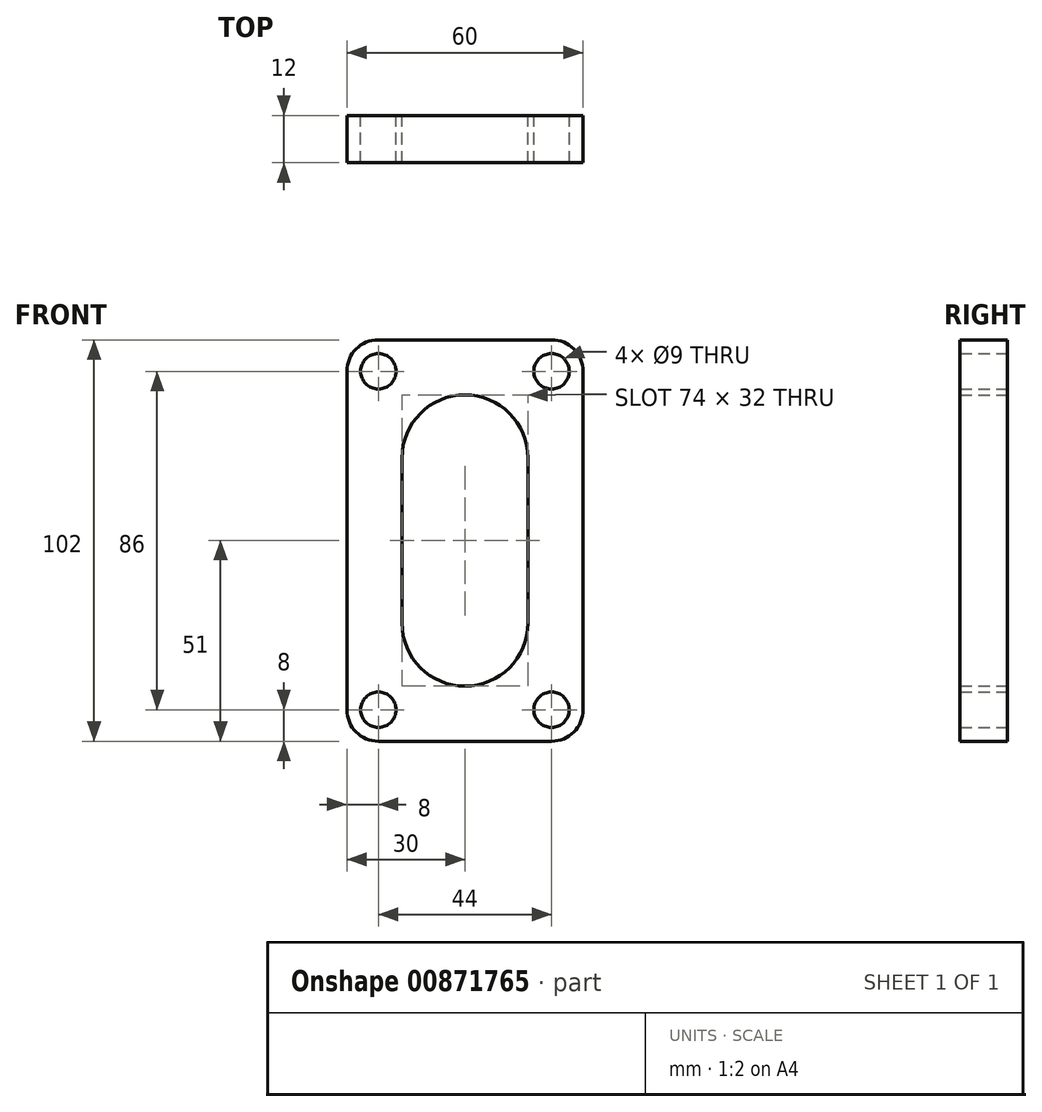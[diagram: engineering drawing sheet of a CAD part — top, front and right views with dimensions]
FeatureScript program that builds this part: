
annotation { "Feature Type Name" : "Feature", "Feature Type Description" : "" }
export const myFeature = defineFeature(function(context is Context, id is Id, definition is map)
    precondition{}
    {
        {
            var Q0;
            Q0=qCreatedBy(makeId("Front.planeOp"),FACE);
            var sketch = newSketch(context, id + "F0", { "sketchPlane" : qUnion([Q0])});
            skLineSegment(sketch, "E0.bottom", {"start": v(-22, 51) * mm, "end": v(22, 51) * mm});
            skLineSegment(sketch, "E0.top", {"start": v(-22, -51) * mm, "end": v(22, -51) * mm});
            skLineSegment(sketch, "E0.left", {"start": v(-30, 43) * mm, "end": v(-30, -43) * mm});
            skLineSegment(sketch, "E0.right", {"start": v(30, 43) * mm, "end": v(30, -43) * mm});
            skPoint(sketch, "E0.middle", {"position": v(0, 0) * mm});
            skArc(sketch, "E1", {"start": v(16, 21) * mm, "mid": v(0, 37) * mm, "end": v(-16, 21) * mm});
            skArc(sketch, "E2", {"start": v(-16, -21) * mm, "mid": v(0, -37) * mm, "end": v(16, -21) * mm});
            skLineSegment(sketch, "E3.left", {"start": v(-16, 21) * mm, "end": v(-16, -21) * mm});
            skLineSegment(sketch, "E3.right", {"start": v(16, 21) * mm, "end": v(16, -21) * mm});
            skPoint(sketch, "E4.visualSharp", {"position": v(-30, 51) * mm});
            skArc(sketch, "E4.filletArc", {"start": v(-22, 51) * mm, "mid": v(-27.66, 48.66) * mm, "end": v(-30, 43) * mm});
            skPoint(sketch, "E5.visualSharp", {"position": v(30, 51) * mm});
            skArc(sketch, "E5.filletArc", {"start": v(30, 43) * mm, "mid": v(27.66, 48.66) * mm, "end": v(22, 51) * mm});
            skPoint(sketch, "E6.visualSharp", {"position": v(30, -51) * mm});
            skArc(sketch, "E6.filletArc", {"start": v(22, -51) * mm, "mid": v(27.66, -48.66) * mm, "end": v(30, -43) * mm});
            skPoint(sketch, "E7.visualSharp", {"position": v(-30, -51) * mm});
            skArc(sketch, "E7.filletArc", {"start": v(-30, -43) * mm, "mid": v(-27.66, -48.66) * mm, "end": v(-22, -51) * mm});
            skCircle(sketch, "E8", {"center": v(-22, 43) * mm, "radius": 4.5 * mm});
            skCircle(sketch, "E9", {"center": v(22, 43) * mm, "radius": 4.5 * mm});
            skCircle(sketch, "E10", {"center": v(22, -43) * mm, "radius": 4.5 * mm});
            skCircle(sketch, "E11", {"center": v(-22, -43) * mm, "radius": 4.5 * mm});
            skSolve(sketch);
        }
        {
            var Q0;
            Q0 = qSketchRegion(id + "F0", true);
            extrude(context, id + "F1", {"entities" : qUnion([Q0]), "depth" : 12 * mm, "offsetDistance" : 25 * mm});
        }
    });
